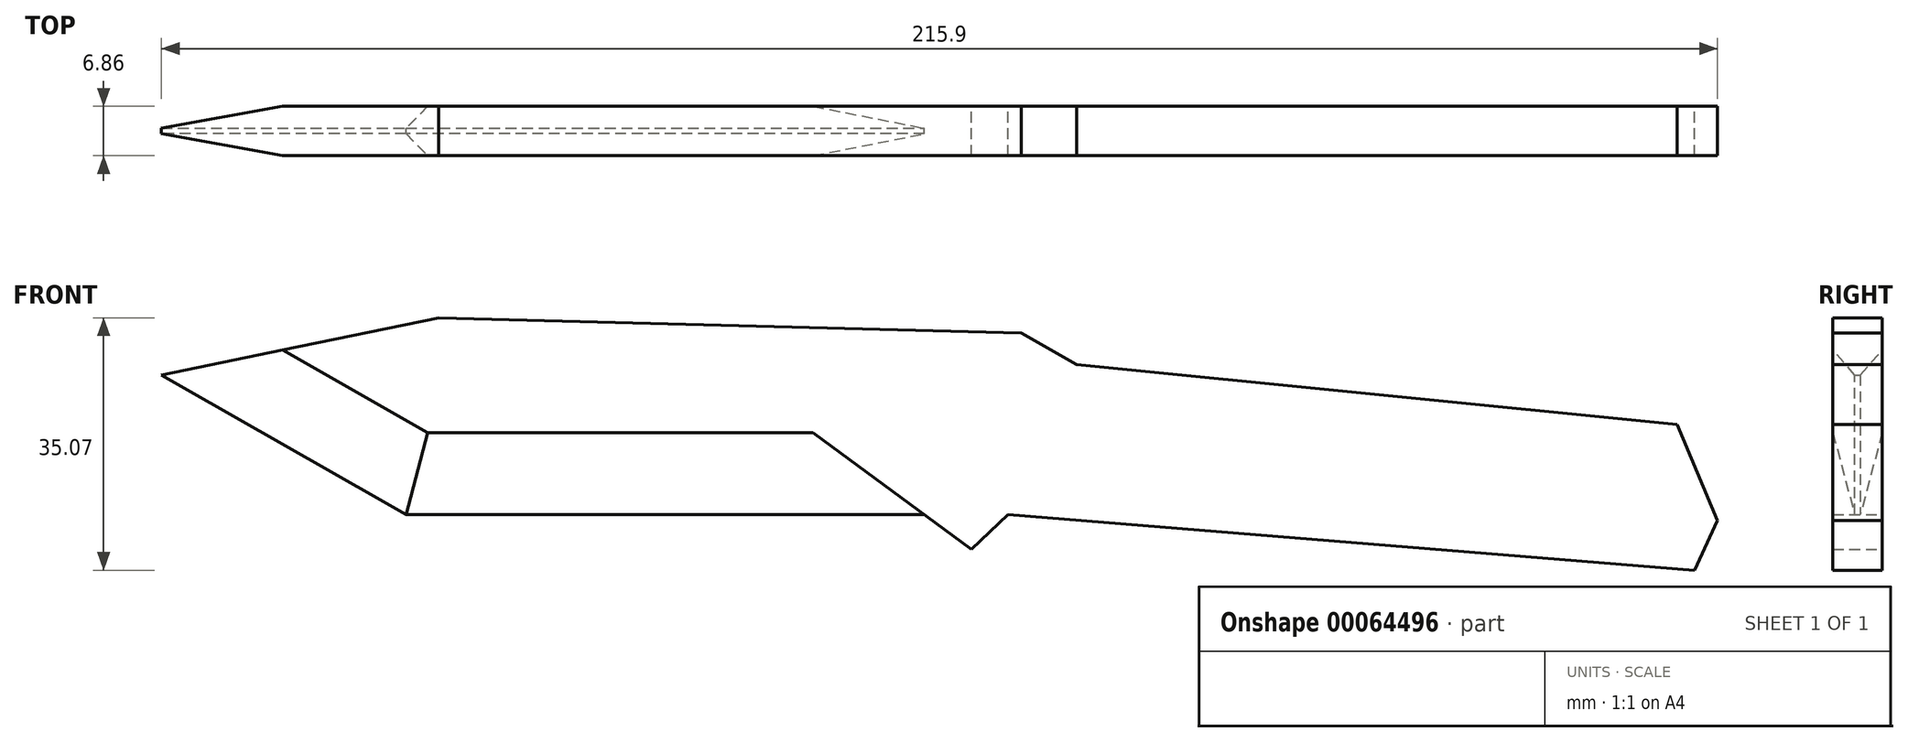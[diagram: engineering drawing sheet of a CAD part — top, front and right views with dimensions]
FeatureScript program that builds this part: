
annotation { "Feature Type Name" : "Feature", "Feature Type Description" : "" }
export const myFeature = defineFeature(function(context is Context, id is Id, definition is map)
    precondition{}
    {
        {
            var Q0;
            Q0=qCreatedBy(makeId("Front.planeOp"),FACE);
            var sketch = newSketch(context, id + "F0", { "sketchPlane" : qUnion([Q0])});
            skLineSegment(sketch, "E0", {"start": v(-91.52, 27.14) * mm, "end": v(-57.57, 7.74) * mm});
            skLineSegment(sketch, "E1", {"start": v(-57.57, 7.74) * mm, "end": v(25.94, 7.74) * mm});
            skLineSegment(sketch, "E2", {"start": v(25.94, 7.74) * mm, "end": v(121.19, 0) * mm});
            skLineSegment(sketch, "E3", {"start": v(121.19, 0) * mm, "end": v(124.38, 6.9) * mm});
            skLineSegment(sketch, "E4", {"start": v(124.38, 6.9) * mm, "end": v(118.8, 20.26) * mm});
            skLineSegment(sketch, "E5", {"start": v(118.8, 20.26) * mm, "end": v(35.45, 28.6) * mm});
            skLineSegment(sketch, "E6", {"start": v(35.45, 28.6) * mm, "end": v(27.8, 32.96) * mm});
            skLineSegment(sketch, "E7", {"start": v(27.8, 32.96) * mm, "end": v(-53.03, 35.07) * mm});
            skLineSegment(sketch, "E8", {"start": v(-53.03, 35.07) * mm, "end": v(-91.52, 27.14) * mm});
            skLineSegment(sketch, "E9", {"start": v(14.34, 7.74) * mm, "end": v(20.86, 2.94) * mm});
            skLineSegment(sketch, "E10", {"start": v(20.86, 2.94) * mm, "end": v(25.94, 7.74) * mm});
            skSolve(sketch);
        }
        {
            var Q0;
            {var subQ2=sQuery(id+"F0.wireOp",EDGE,"E9");Q0=makeQuery(id+"F0.imprint","IMPRINT",FACE,{"disambiguationData":[TD([[makeQuery(id+"F0.imprint","IMPRINT",EDGE,{"derivedFrom":subQ2}),1.0]])]});}
            var Q1;
            {var subQ2=sQuery(id+"F0.wireOp",EDGE,"E0");Q1=makeQuery(id+"F0.imprint","IMPRINT",FACE,{"disambiguationData":[TD([[makeQuery(id+"F0.imprint","IMPRINT",EDGE,{"derivedFrom":subQ2}),1.0]])]});}
            extrude(context, id + "F1", {"entities" : qUnion([Q0, Q1]), "depth" : 6.86 * mm});
        }
        {
            var Q0;
            Q0=makeQuery(id+"F1.opExtrude","SWEPT_FACE",FACE,{"disambiguationData":[OSD([sQuery(id+"F0.wireOp",EDGE,"E0")])]});
            var sketch = newSketch(context, id + "F2", { "sketchPlane" : qUnion([Q0])});
            skPoint(sketch, "E11", {"position": v(-92.93, 3.43) * mm});
            skPoint(sketch, "E12", {"position": v(-53.83, 3.43) * mm});
            skLineSegment(sketch, "E13", {"start": v(-92.93, 3.43) * mm, "end": v(-53.83, 3.43) * mm});
            skSolve(sketch);
        }
        {
            var Q0;
            Q0=makeQuery(id+"F1.opExtrude","SWEPT_FACE",FACE,{"disambiguationData":[OSD([sQuery(id+"F0.wireOp",EDGE,"E1")])]});
            var sketch = newSketch(context, id + "F3", { "sketchPlane" : qUnion([Q0])});
            skPoint(sketch, "E14", {"position": v(14.34, 3.43) * mm});
            skLineSegment(sketch, "E15", {"start": v(-57.57, 3.43) * mm, "end": v(14.34, 3.43) * mm});
            skSolve(sketch);
        }
        {
            var Q0;
            Q0=makeQuery(id+"F1.opExtrude","CAP_EDGE",EDGE,{"disambiguationData":[OSD([sQuery(id+"F0.wireOp",EDGE,"E0")])],"isStart":false});
            var Q1;
            Q1=makeQuery(id+"F1.opExtrude","CAP_EDGE",EDGE,{"disambiguationData":[OSD([sQuery(id+"F0.wireOp",EDGE,"E1")])],"isStart":false});
            chamfer(context, id + "F4", {"entities" : qUnion([Q0, Q1]), "chamferType" : ChamferType.OFFSET_ANGLE, "width" : 3.05 * mm, "oppositeDirection" : true, "angle" : 75 * degree, "tangentPropagation" : true});
        }
        {
            var Q0;
            Q0=makeQuery(id+"F1.opExtrude","CAP_EDGE",EDGE,{"disambiguationData":[OSD([sQuery(id+"F0.wireOp",EDGE,"E0")])],"isStart":true});
            var Q1;
            Q1=makeQuery(id+"F1.opExtrude","CAP_EDGE",EDGE,{"disambiguationData":[OSD([sQuery(id+"F0.wireOp",EDGE,"E1")])],"isStart":true});
            chamfer(context, id + "F5", {"entities" : qUnion([Q0, Q1]), "chamferType" : ChamferType.OFFSET_ANGLE, "width" : 3.05 * mm, "oppositeDirection" : false, "angle" : 75 * degree, "tangentPropagation" : true});
        }
    });
